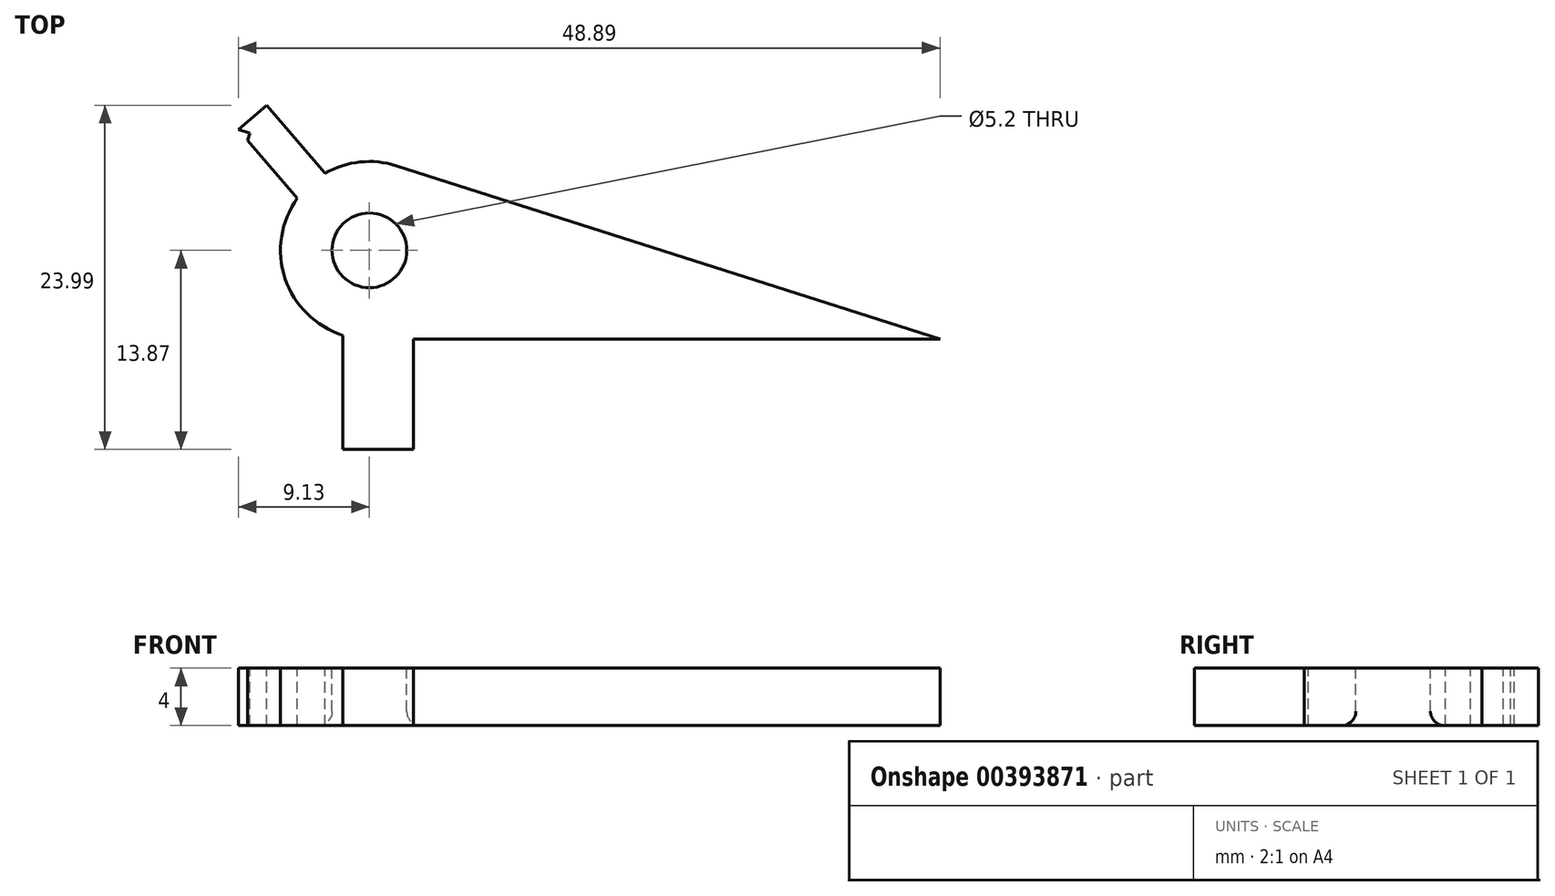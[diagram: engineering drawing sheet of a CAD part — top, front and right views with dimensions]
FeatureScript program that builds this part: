
annotation { "Feature Type Name" : "Feature", "Feature Type Description" : "" }
export const myFeature = defineFeature(function(context is Context, id is Id, definition is map)
    precondition{}
    {
        {
            var Q0;
            Q0=qCreatedBy(makeId("Top.planeOp"),FACE);
            var sketch = newSketch(context, id + "F0", { "sketchPlane" : qUnion([Q0])});
            skArc(sketch, "E0", {"start": v(1.88, 5.9) * mm, "mid": v(-5.9, 1.87) * mm, "end": v(-1.85, -5.91) * mm});
            skLineSegment(sketch, "E1", {"start": v(3.07, -6.2) * mm, "end": v(39.76, -6.2) * mm});
            skLineSegment(sketch, "E2", {"start": v(-1.85, -5.91) * mm, "end": v(-1.85, -13.87) * mm});
            skLineSegment(sketch, "E3", {"start": v(-1.85, -13.87) * mm, "end": v(3.07, -13.87) * mm});
            skLineSegment(sketch, "E4", {"start": v(3.07, -13.87) * mm, "end": v(3.07, -6.2) * mm});
            skPoint(sketch, "E5.end.orphan", {"position": v(0, 6.5) * mm});
            skLineSegment(sketch, "E6", {"start": v(39.76, -6.2) * mm, "end": v(1.88, 5.9) * mm});
            skPoint(sketch, "E7.start.orphan", {"position": v(0, -6.2) * mm});
            skSolve(sketch);
        }
        {
            var Q0;
            Q0=qCreatedBy(makeId("Top.planeOp"),FACE);
            var sketch = newSketch(context, id + "F1", { "sketchPlane" : qUnion([Q0])});
            skCircle(sketch, "E8", {"center": v(0, 0) * mm, "radius": 2.6 * mm});
            skSolve(sketch);
        }
        {
            var Q0;
            Q0=makeQuery(id+"F0.imprint","IMPRINT",FACE,{"disambiguationData":[TD([[makeQuery(id+"F0.imprint","IMPRINT",EDGE,{"derivedFrom":sQuery(id+"F0.wireOp",EDGE,"E0")}),1.0]])]});
            extrude(context, id + "F2", {"entities" : qUnion([Q0]), "oppositeDirection" : true, "depth" : 4 * mm});
        }
        {
            var Q0;
            Q0=makeQuery(id+"F1.imprint","IMPRINT",FACE,{"disambiguationData":[TD([[makeQuery(id+"F1.imprint","IMPRINT",EDGE,{"derivedFrom":sQuery(id+"F1.wireOp",EDGE,"E8")}),1.0]])]});
            extrude(context, id + "F3", {"entities" : qUnion([Q0]), "operationType" : NewBodyOperationType.REMOVE, "oppositeDirection" : true, "depth" : 5 * mm});
        }
        {
            var Q0;
            Q0=makeQuery(id+"F3.boolean.opBoolean","COPY",EDGE,{"derivedFrom":makeQuery(id+"F3.opExtrude","CAP_EDGE",EDGE,{"disambiguationData":[OSD([sQuery(id+"F1.wireOp",EDGE,"E8")])],"isStart":true})});
            var Q1;
            Q1=makeQuery(id+"F3.boolean.opBoolean","INTERSECT",EDGE,{"derivedFrom":[makeQuery(id+"F2.opExtrude","CAP_FACE",FACE,{"disambiguationData":[OSD([sQuery(id+"F0.wireOp",EDGE,"E0"),sQuery(id+"F0.wireOp",EDGE,"E1"),sQuery(id+"F0.wireOp",EDGE,"E2"),sQuery(id+"F0.wireOp",EDGE,"E3"),sQuery(id+"F0.wireOp",EDGE,"E4"),sQuery(id+"F0.wireOp",EDGE,"E6")])],"isStart":false}),makeQuery(id+"F3.opExtrude","SWEPT_FACE",FACE,{"disambiguationData":[OSD([sQuery(id+"F1.wireOp",EDGE,"E8")])]})]});
            fillet(context, id + "F4", {"entities" : qUnion([Q0, Q1]), "radius" : 1 * mm, "tangentPropagation" : true, "allowEdgeOverflow" : false});
        }
        {
            var Q0;
            Q0=qCreatedBy(makeId("Top.planeOp"),FACE);
            var sketch = newSketch(context, id + "F5", { "sketchPlane" : qUnion([Q0])});
            skLineSegment(sketch, "E9", {"start": v(-3.06, 5.35) * mm, "end": v(-7.16, 10.12) * mm});
            skLineSegment(sketch, "E10", {"start": v(-7.16, 10.12) * mm, "end": v(-9.13, 8.42) * mm});
            skLineSegment(sketch, "E11", {"start": v(-8.48, 7.67) * mm, "end": v(-4.7, 3.28) * mm});
            skLineSegment(sketch, "E12", {"start": v(-4.7, 3.28) * mm, "end": v(-3.06, 5.35) * mm});
            skLineSegment(sketch, "E13", {"start": v(-9.13, 8.42) * mm, "end": v(-8.33, 8.18) * mm});
            skLineSegment(sketch, "E14", {"start": v(-8.33, 8.18) * mm, "end": v(-8.48, 7.67) * mm});
            skSolve(sketch);
        }
        {
            var Q0;
            Q0 = qSketchRegion(id + "F5", true);
            extrude(context, id + "F6", {"entities" : qUnion([Q0]), "operationType" : NewBodyOperationType.ADD, "oppositeDirection" : true, "depth" : 4 * mm});
        }
    });
